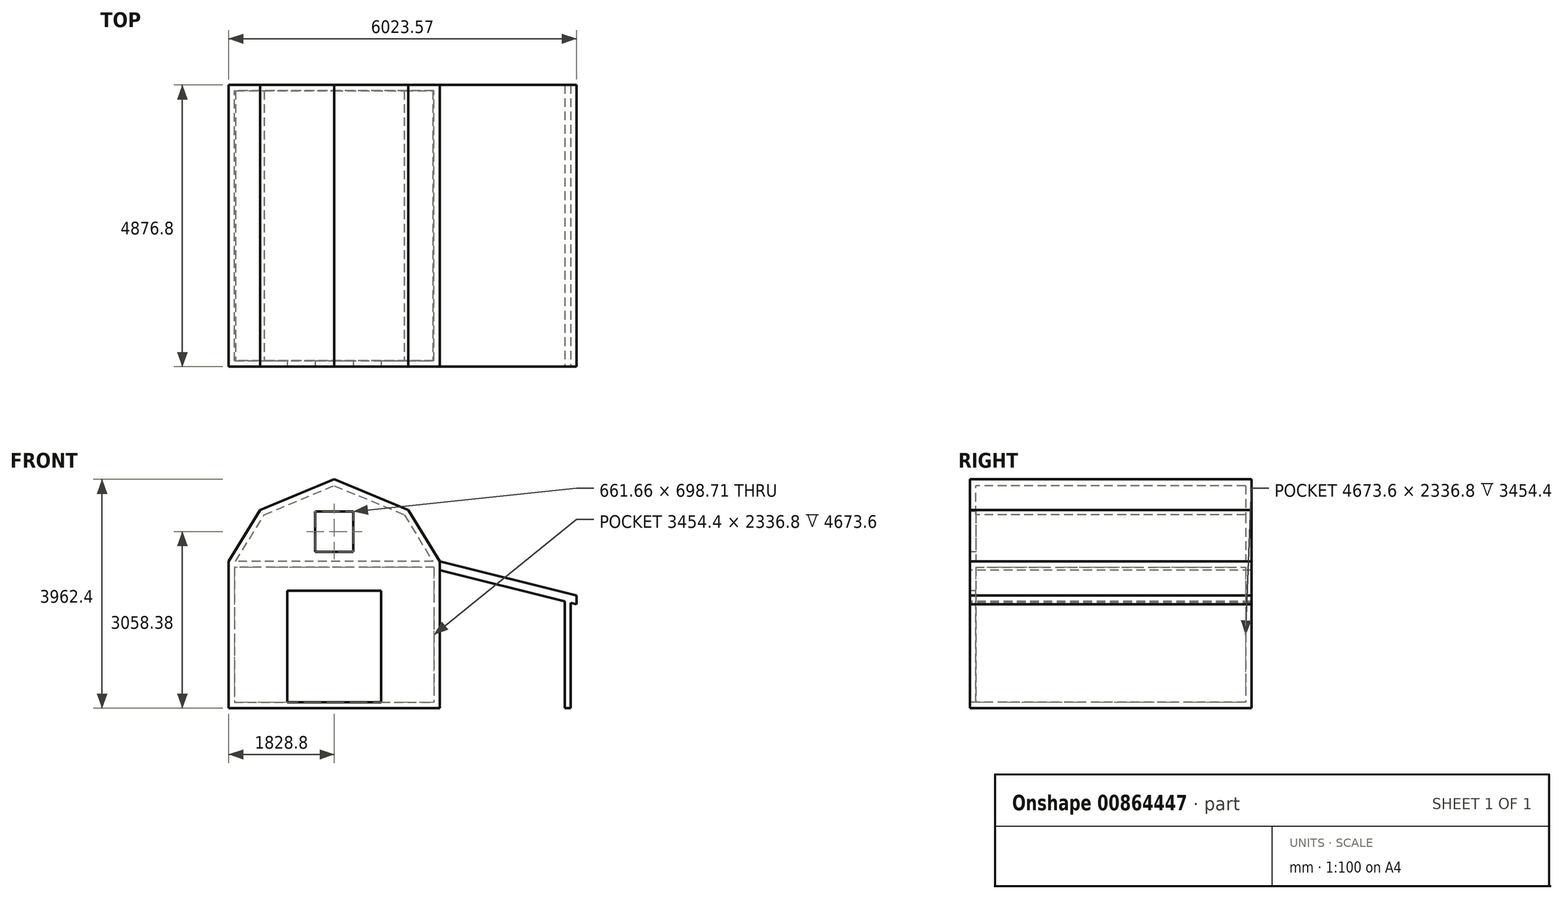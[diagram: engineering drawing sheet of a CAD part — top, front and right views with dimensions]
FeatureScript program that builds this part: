
annotation { "Feature Type Name" : "Feature", "Feature Type Description" : "" }
export const myFeature = defineFeature(function(context is Context, id is Id, definition is map)
    precondition{}
    {
        {
            var Q0;
            Q0=qCreatedBy(makeId("Top.planeOp"),FACE);
            var sketch = newSketch(context, id + "F0", { "sketchPlane" : qUnion([Q0])});
            skLineSegment(sketch, "E0.bottom", {"start": v(-1828.8, 2438.4) * mm, "end": v(1828.8, 2438.4) * mm});
            skLineSegment(sketch, "E0.top", {"start": v(-1828.8, -2438.4) * mm, "end": v(1828.8, -2438.4) * mm});
            skLineSegment(sketch, "E0.left", {"start": v(-1828.8, 2438.4) * mm, "end": v(-1828.8, -2438.4) * mm});
            skLineSegment(sketch, "E0.right", {"start": v(1828.8, 2438.4) * mm, "end": v(1828.8, -2438.4) * mm});
            skPoint(sketch, "E0.middle", {"position": v(0, 0) * mm});
            skSolve(sketch);
        }
        {
            var Q0;
            Q0=makeQuery(id+"F0.imprint","IMPRINT",FACE,{"disambiguationData":[TD([[makeQuery(id+"F0.imprint","IMPRINT",EDGE,{"derivedFrom":sQuery(id+"F0.wireOp",EDGE,"E0.bottom")}),-1.0]])]});
            extrude(context, id + "F1", {"entities" : qUnion([Q0]), "oppositeDirection" : true, "depth" : 101.6 * mm, "offsetDistance" : 30.48 * mm});
        }
        {
            var Q0;
            Q0=makeQuery(id+"F1.opExtrude","CAP_FACE",FACE,{"disambiguationData":[OSD([sQuery(id+"F0.wireOp",EDGE,"E0.bottom"),sQuery(id+"F0.wireOp",EDGE,"E0.top"),sQuery(id+"F0.wireOp",EDGE,"E0.left"),sQuery(id+"F0.wireOp",EDGE,"E0.right")])],"isStart":true});
            var sketch = newSketch(context, id + "F2", { "sketchPlane" : qUnion([Q0])});
            skLineSegment(sketch, "E1.0", {"start": v(-1727.2, 2336.8) * mm, "end": v(1727.2, 2336.8) * mm});
            skLineSegment(sketch, "E1.1", {"start": v(-1727.2, 2336.8) * mm, "end": v(-1727.2, -2336.8) * mm});
            skLineSegment(sketch, "E1.2", {"start": v(-1727.2, -2336.8) * mm, "end": v(1727.2, -2336.8) * mm});
            skLineSegment(sketch, "E1.3", {"start": v(1727.2, 2336.8) * mm, "end": v(1727.2, -2336.8) * mm});
            skSolve(sketch);
        }
        {
            var Q0;
            Q0=makeQuery(id+"F2.imprint","IMPRINT",FACE,{"disambiguationData":[TD([[makeQuery(id+"F2.imprint","IMPRINT",EDGE,{"derivedFrom":sQuery(id+"F2.wireOp",EDGE,"E1.0")}),1.0]])]});
            extrude(context, id + "F3", {"entities" : qUnion([Q0]), "operationType" : NewBodyOperationType.ADD, "depth" : 2438.4 * mm, "offsetDistance" : 30.48 * mm});
        }
        {
            var Q0;
            {var subQ0=sQuery(id+"F0.wireOp",EDGE,"E0.top");Q0=makeQuery(id+"F3.boolean.opBoolean","MERGE",FACE,{"derivedFrom":[makeQuery(id+"F1.opExtrude","SWEPT_FACE",FACE,{"disambiguationData":[OSD([subQ0])]}),makeQuery(id+"F3.opExtrude","SWEPT_FACE",FACE,{"disambiguationData":[OSD([subQ0])]})]});}
            var sketch = newSketch(context, id + "F4", { "sketchPlane" : qUnion([Q0])});
            skLineSegment(sketch, "E2.bottom", {"start": v(0, 0) * mm, "end": v(812.8, 0) * mm});
            skLineSegment(sketch, "E2.top", {"start": v(0, 1930.4) * mm, "end": v(812.8, 1930.4) * mm});
            skLineSegment(sketch, "E2.left", {"start": v(0, 0) * mm, "end": v(0, 1930.4) * mm});
            skLineSegment(sketch, "E2.right", {"start": v(812.8, 0) * mm, "end": v(812.8, 1930.4) * mm});
            skLineSegment(sketch, "E3.bottom", {"start": v(0, 0) * mm, "end": v(-812.8, 0) * mm});
            skLineSegment(sketch, "E3.top", {"start": v(0, 1930.4) * mm, "end": v(-812.8, 1930.4) * mm});
            skLineSegment(sketch, "E3.right", {"start": v(-812.8, 0) * mm, "end": v(-812.8, 1930.4) * mm});
            skSolve(sketch);
        }
        {
            var Q0;
            Q0=makeQuery(id+"F4.imprint","IMPRINT",FACE,{"disambiguationData":[TD([[makeQuery(id+"F4.imprint","IMPRINT",EDGE,{"derivedFrom":sQuery(id+"F4.wireOp",EDGE,"E3.bottom")}),-1.0]])]});
            var Q1;
            Q1=makeQuery(id+"F4.imprint","IMPRINT",FACE,{"disambiguationData":[TD([[makeQuery(id+"F4.imprint","IMPRINT",EDGE,{"derivedFrom":sQuery(id+"F4.wireOp",EDGE,"E2.bottom")}),1.0]])]});
            extrude(context, id + "F5", {"entities" : qUnion([Q0, Q1]), "operationType" : NewBodyOperationType.REMOVE, "oppositeDirection" : true, "depth" : 101.6 * mm, "offsetDistance" : 30.48 * mm});
        }
        {
            var Q0;
            {var subQ0=sQuery(id+"F0.wireOp",EDGE,"E0.top");Q0=makeQuery(id+"F3.boolean.opBoolean","MERGE",FACE,{"derivedFrom":[makeQuery(id+"F1.opExtrude","SWEPT_FACE",FACE,{"disambiguationData":[OSD([subQ0])]}),makeQuery(id+"F3.opExtrude","SWEPT_FACE",FACE,{"disambiguationData":[OSD([subQ0])]})]});}
            var sketch = newSketch(context, id + "F6", { "sketchPlane" : qUnion([Q0])});
            skLineSegment(sketch, "E4", {"start": v(-1828.8, 2438.4) * mm, "end": v(-1282.5, 3330.3) * mm});
            skLineSegment(sketch, "E5", {"start": v(-1282.5, 3330.3) * mm, "end": v(0, 3860.8) * mm});
            skLineSegment(sketch, "E6", {"start": v(0, 3860.8) * mm, "end": v(1282.5, 3330.3) * mm});
            skLineSegment(sketch, "E7", {"start": v(1282.5, 3330.3) * mm, "end": v(1828.8, 2438.4) * mm});
            skLineSegment(sketch, "E8.0", {"start": v(1213.12, 3249.05) * mm, "end": v(1709.66, 2438.4) * mm});
            skLineSegment(sketch, "E8.1", {"start": v(0, 3750.85) * mm, "end": v(1213.12, 3249.05) * mm});
            skLineSegment(sketch, "E8.2", {"start": v(-1213.12, 3249.05) * mm, "end": v(0, 3750.85) * mm});
            skLineSegment(sketch, "E8.3", {"start": v(-1709.66, 2438.4) * mm, "end": v(-1213.12, 3249.05) * mm});
            skLineSegment(sketch, "E9", {"start": v(-1828.8, 2438.4) * mm, "end": v(-1709.66, 2438.4) * mm});
            skLineSegment(sketch, "E10", {"start": v(1709.66, 2438.4) * mm, "end": v(1828.8, 2438.4) * mm});
            skSolve(sketch);
        }
        {
            var Q0;
            Q0=makeQuery(id+"F6.imprint","IMPRINT",FACE,{"disambiguationData":[TD([[makeQuery(id+"F6.imprint","IMPRINT",EDGE,{"derivedFrom":sQuery(id+"F6.wireOp",EDGE,"E4")}),-1.0]])]});
            extrude(context, id + "F7", {"entities" : qUnion([Q0]), "operationType" : NewBodyOperationType.ADD, "oppositeDirection" : true, "depth" : 4876.8 * mm, "offsetDistance" : 30.48 * mm});
        }
        {
            var Q0;
            {var subQ0=sQuery(id+"F0.wireOp",EDGE,"E0.top");Q0=makeQuery(id+"F7.boolean.opBoolean","MERGE",FACE,{"derivedFrom":[makeQuery(id+"F3.boolean.opBoolean","MERGE",FACE,{"derivedFrom":[makeQuery(id+"F1.opExtrude","SWEPT_FACE",FACE,{"disambiguationData":[OSD([subQ0])]}),makeQuery(id+"F3.opExtrude","SWEPT_FACE",FACE,{"disambiguationData":[OSD([subQ0])]})]}),makeQuery(id+"F7.opExtrude","CAP_FACE",FACE,{"disambiguationData":[OSD([sQuery(id+"F6.wireOp",EDGE,"E4"),sQuery(id+"F6.wireOp",EDGE,"E5"),sQuery(id+"F6.wireOp",EDGE,"E6"),sQuery(id+"F6.wireOp",EDGE,"E7"),sQuery(id+"F6.wireOp",EDGE,"E8.0"),sQuery(id+"F6.wireOp",EDGE,"E8.1"),sQuery(id+"F6.wireOp",EDGE,"E8.2"),sQuery(id+"F6.wireOp",EDGE,"E8.3"),sQuery(id+"F6.wireOp",EDGE,"E9"),sQuery(id+"F6.wireOp",EDGE,"E10")])],"isStart":true})]});}
            var sketch = newSketch(context, id + "F8", { "sketchPlane" : qUnion([Q0])});
            skLineSegment(sketch, "E11", {"start": v(-1709.66, 2438.4) * mm, "end": v(-1213.12, 3249.05) * mm});
            skLineSegment(sketch, "E12", {"start": v(-1213.12, 3249.05) * mm, "end": v(0, 3750.85) * mm});
            skLineSegment(sketch, "E13", {"start": v(0, 3750.85) * mm, "end": v(1213.12, 3249.05) * mm});
            skLineSegment(sketch, "E14", {"start": v(1213.12, 3249.05) * mm, "end": v(1709.66, 2438.4) * mm});
            skLineSegment(sketch, "E15", {"start": v(1709.66, 2438.4) * mm, "end": v(-1709.66, 2438.4) * mm});
            skLineSegment(sketch, "E16.bottom", {"start": v(-330.83, 3306.14) * mm, "end": v(330.83, 3306.14) * mm});
            skLineSegment(sketch, "E16.top", {"start": v(-330.83, 2607.43) * mm, "end": v(330.83, 2607.43) * mm});
            skLineSegment(sketch, "E16.left", {"start": v(-330.83, 3306.14) * mm, "end": v(-330.83, 2607.43) * mm});
            skLineSegment(sketch, "E16.right", {"start": v(330.83, 3306.14) * mm, "end": v(330.83, 2607.43) * mm});
            skLineSegment(sketch, "E17", {"start": v(-1213.12, 3249.05) * mm, "end": v(-330.83, 3306.14) * mm});
            skLineSegment(sketch, "E18", {"start": v(1213.12, 3249.05) * mm, "end": v(330.83, 3306.14) * mm});
            skSolve(sketch);
        }
        {
            var Q0;
            Q0=makeQuery(id+"F8.imprint","IMPRINT",FACE,{"disambiguationData":[TD([[makeQuery(id+"F8.imprint","IMPRINT",EDGE,{"derivedFrom":sQuery(id+"F8.wireOp",EDGE,"E11")}),-1.0]])]});
            var Q1;
            Q1=makeQuery(id+"F8.imprint","IMPRINT",FACE,{"disambiguationData":[TD([[makeQuery(id+"F8.imprint","IMPRINT",EDGE,{"derivedFrom":sQuery(id+"F8.wireOp",EDGE,"E12")}),-1.0]])]});
            extrude(context, id + "F9", {"entities" : qUnion([Q0, Q1]), "operationType" : NewBodyOperationType.ADD, "oppositeDirection" : true, "depth" : 101.6 * mm, "offsetDistance" : 30.48 * mm});
        }
        {
            var Q0;
            {var subQ0=sQuery(id+"F0.wireOp",EDGE,"E0.bottom");Q0=makeQuery(id+"F7.boolean.opBoolean","MERGE",FACE,{"derivedFrom":[makeQuery(id+"F3.boolean.opBoolean","MERGE",FACE,{"derivedFrom":[makeQuery(id+"F1.opExtrude","SWEPT_FACE",FACE,{"disambiguationData":[OSD([subQ0])]}),makeQuery(id+"F3.opExtrude","SWEPT_FACE",FACE,{"disambiguationData":[OSD([subQ0])]})]}),makeQuery(id+"F7.opExtrude","CAP_FACE",FACE,{"disambiguationData":[OSD([sQuery(id+"F6.wireOp",EDGE,"E4"),sQuery(id+"F6.wireOp",EDGE,"E5"),sQuery(id+"F6.wireOp",EDGE,"E6"),sQuery(id+"F6.wireOp",EDGE,"E7"),sQuery(id+"F6.wireOp",EDGE,"E8.0"),sQuery(id+"F6.wireOp",EDGE,"E8.1"),sQuery(id+"F6.wireOp",EDGE,"E8.2"),sQuery(id+"F6.wireOp",EDGE,"E8.3"),sQuery(id+"F6.wireOp",EDGE,"E9"),sQuery(id+"F6.wireOp",EDGE,"E10")])],"isStart":false})]});}
            var sketch = newSketch(context, id + "F10", { "sketchPlane" : qUnion([Q0])});
            skLineSegment(sketch, "E19", {"start": v(-1709.66, 2438.4) * mm, "end": v(-1213.12, 3249.05) * mm});
            skLineSegment(sketch, "E20", {"start": v(-1213.12, 3249.05) * mm, "end": v(0, 3750.85) * mm});
            skLineSegment(sketch, "E21", {"start": v(0, 3750.85) * mm, "end": v(1213.12, 3249.05) * mm});
            skLineSegment(sketch, "E22", {"start": v(1213.12, 3249.05) * mm, "end": v(1709.66, 2438.4) * mm});
            skLineSegment(sketch, "E23", {"start": v(1709.66, 2438.4) * mm, "end": v(-1709.66, 2438.4) * mm});
            skSolve(sketch);
        }
        {
            var Q0;
            Q0=makeQuery(id+"F10.imprint","IMPRINT",FACE,{"disambiguationData":[TD([[makeQuery(id+"F10.imprint","IMPRINT",EDGE,{"derivedFrom":sQuery(id+"F10.wireOp",EDGE,"E19")}),1.0]])]});
            extrude(context, id + "F11", {"entities" : qUnion([Q0]), "operationType" : NewBodyOperationType.ADD, "oppositeDirection" : true, "depth" : 101.6 * mm, "offsetDistance" : 30.48 * mm});
        }
        {
            var Q0;
            {var subQ0=sQuery(id+"F0.wireOp",EDGE,"E0.top");Q0=makeQuery(id+"F9.boolean.opBoolean","MERGE",FACE,{"derivedFrom":[makeQuery(id+"F7.boolean.opBoolean","MERGE",FACE,{"derivedFrom":[makeQuery(id+"F3.boolean.opBoolean","MERGE",FACE,{"derivedFrom":[makeQuery(id+"F1.opExtrude","SWEPT_FACE",FACE,{"disambiguationData":[OSD([subQ0])]}),makeQuery(id+"F3.opExtrude","SWEPT_FACE",FACE,{"disambiguationData":[OSD([subQ0])]})]}),makeQuery(id+"F7.opExtrude","CAP_FACE",FACE,{"disambiguationData":[OSD([sQuery(id+"F6.wireOp",EDGE,"E4"),sQuery(id+"F6.wireOp",EDGE,"E5"),sQuery(id+"F6.wireOp",EDGE,"E6"),sQuery(id+"F6.wireOp",EDGE,"E7"),sQuery(id+"F6.wireOp",EDGE,"E8.0"),sQuery(id+"F6.wireOp",EDGE,"E8.1"),sQuery(id+"F6.wireOp",EDGE,"E8.2"),sQuery(id+"F6.wireOp",EDGE,"E8.3"),sQuery(id+"F6.wireOp",EDGE,"E9"),sQuery(id+"F6.wireOp",EDGE,"E10")])],"isStart":true})]}),makeQuery(id+"F9.opExtrude","CAP_FACE",FACE,{"disambiguationData":[OSD([sQuery(id+"F8.wireOp",EDGE,"E11"),sQuery(id+"F8.wireOp",EDGE,"E12"),sQuery(id+"F8.wireOp",EDGE,"E13"),sQuery(id+"F8.wireOp",EDGE,"E14"),sQuery(id+"F8.wireOp",EDGE,"E15"),sQuery(id+"F8.wireOp",EDGE,"E16.bottom"),sQuery(id+"F8.wireOp",EDGE,"E16.top"),sQuery(id+"F8.wireOp",EDGE,"E16.left"),sQuery(id+"F8.wireOp",EDGE,"E16.right")])],"isStart":true})]});}
            var sketch = newSketch(context, id + "F12", { "sketchPlane" : qUnion([Q0])});
            skLineSegment(sketch, "E24.bottom", {"start": v(-1828.8, 2438.4) * mm, "end": v(1828.8, 2438.4) * mm});
            skLineSegment(sketch, "E24.top", {"start": v(-1828.8, 2336.8) * mm, "end": v(1828.8, 2336.8) * mm});
            skLineSegment(sketch, "E24.left", {"start": v(-1828.8, 2438.4) * mm, "end": v(-1828.8, 2336.8) * mm});
            skLineSegment(sketch, "E24.right", {"start": v(1828.8, 2438.4) * mm, "end": v(1828.8, 2336.8) * mm});
            skSolve(sketch);
        }
        {
            var Q0;
            Q0=makeQuery(id+"F12.imprint","IMPRINT",FACE,{"disambiguationData":[TD([[makeQuery(id+"F12.imprint","IMPRINT",EDGE,{"derivedFrom":sQuery(id+"F12.wireOp",EDGE,"E24.bottom")}),-1.0]])]});
            extrude(context, id + "F13", {"entities" : qUnion([Q0]), "operationType" : NewBodyOperationType.ADD, "oppositeDirection" : true, "depth" : 4876.8 * mm, "offsetDistance" : 30.48 * mm});
        }
        {
            var Q0;
            {var subQ0=sQuery(id+"F0.wireOp",EDGE,"E0.top");Q0=makeQuery(id+"F9.boolean.opBoolean","MERGE",FACE,{"derivedFrom":[makeQuery(id+"F7.boolean.opBoolean","MERGE",FACE,{"derivedFrom":[makeQuery(id+"F3.boolean.opBoolean","MERGE",FACE,{"derivedFrom":[makeQuery(id+"F1.opExtrude","SWEPT_FACE",FACE,{"disambiguationData":[OSD([subQ0])]}),makeQuery(id+"F3.opExtrude","SWEPT_FACE",FACE,{"disambiguationData":[OSD([subQ0])]})]}),makeQuery(id+"F7.opExtrude","CAP_FACE",FACE,{"disambiguationData":[OSD([sQuery(id+"F6.wireOp",EDGE,"E4"),sQuery(id+"F6.wireOp",EDGE,"E5"),sQuery(id+"F6.wireOp",EDGE,"E6"),sQuery(id+"F6.wireOp",EDGE,"E7"),sQuery(id+"F6.wireOp",EDGE,"E8.0"),sQuery(id+"F6.wireOp",EDGE,"E8.1"),sQuery(id+"F6.wireOp",EDGE,"E8.2"),sQuery(id+"F6.wireOp",EDGE,"E8.3"),sQuery(id+"F6.wireOp",EDGE,"E9"),sQuery(id+"F6.wireOp",EDGE,"E10")])],"isStart":true})]}),makeQuery(id+"F9.opExtrude","CAP_FACE",FACE,{"disambiguationData":[OSD([sQuery(id+"F8.wireOp",EDGE,"E11"),sQuery(id+"F8.wireOp",EDGE,"E12"),sQuery(id+"F8.wireOp",EDGE,"E13"),sQuery(id+"F8.wireOp",EDGE,"E14"),sQuery(id+"F8.wireOp",EDGE,"E15"),sQuery(id+"F8.wireOp",EDGE,"E16.bottom"),sQuery(id+"F8.wireOp",EDGE,"E16.top"),sQuery(id+"F8.wireOp",EDGE,"E16.left"),sQuery(id+"F8.wireOp",EDGE,"E16.right")])],"isStart":true})]});}
            var sketch = newSketch(context, id + "F14", { "sketchPlane" : qUnion([Q0])});
            skLineSegment(sketch, "E25.bottom", {"start": v(1828.8, 2438.4) * mm, "end": v(4194.77, 1848.5) * mm});
            skLineSegment(sketch, "E26", {"start": v(1828.8, 2438.4) * mm, "end": v(1828.8, 2286) * mm});
            skLineSegment(sketch, "E27", {"start": v(1828.8, 2286) * mm, "end": v(4194.77, 1696.1) * mm});
            skLineSegment(sketch, "E28", {"start": v(4194.77, 1696.1) * mm, "end": v(4194.77, 1848.5) * mm});
            skSolve(sketch);
        }
        {
            var Q0;
            Q0=makeQuery(id+"F14.imprint","IMPRINT",FACE,{"disambiguationData":[TD([[makeQuery(id+"F14.imprint","IMPRINT",EDGE,{"derivedFrom":sQuery(id+"F14.wireOp",EDGE,"E25.bottom")}),-1.0]])]});
            extrude(context, id + "F15", {"entities" : qUnion([Q0]), "oppositeDirection" : true, "depth" : 4876.8 * mm, "offsetDistance" : 30.48 * mm});
        }
        {
            var Q0;
            Q0=makeQuery(id+"F15.opExtrude","SWEPT_BODY",BODY,{"disambiguationData":[OSD([sQuery(id+"F14.wireOp",EDGE,"E25.bottom"),sQuery(id+"F14.wireOp",EDGE,"E26"),sQuery(id+"F14.wireOp",EDGE,"E27"),sQuery(id+"F14.wireOp",EDGE,"E28")])]});
            deleteBodies(context, id + "F16", {"entities" : qUnion([Q0])});
        }
        {
            var Q0;
            {var subQ0=sQuery(id+"F0.wireOp",EDGE,"E0.top");Q0=makeQuery(id+"F9.boolean.opBoolean","MERGE",FACE,{"derivedFrom":[makeQuery(id+"F7.boolean.opBoolean","MERGE",FACE,{"derivedFrom":[makeQuery(id+"F3.boolean.opBoolean","MERGE",FACE,{"derivedFrom":[makeQuery(id+"F1.opExtrude","SWEPT_FACE",FACE,{"disambiguationData":[OSD([subQ0])]}),makeQuery(id+"F3.opExtrude","SWEPT_FACE",FACE,{"disambiguationData":[OSD([subQ0])]})]}),makeQuery(id+"F7.opExtrude","CAP_FACE",FACE,{"disambiguationData":[OSD([sQuery(id+"F6.wireOp",EDGE,"E4"),sQuery(id+"F6.wireOp",EDGE,"E5"),sQuery(id+"F6.wireOp",EDGE,"E6"),sQuery(id+"F6.wireOp",EDGE,"E7"),sQuery(id+"F6.wireOp",EDGE,"E8.0"),sQuery(id+"F6.wireOp",EDGE,"E8.1"),sQuery(id+"F6.wireOp",EDGE,"E8.2"),sQuery(id+"F6.wireOp",EDGE,"E8.3"),sQuery(id+"F6.wireOp",EDGE,"E9"),sQuery(id+"F6.wireOp",EDGE,"E10")])],"isStart":true})]}),makeQuery(id+"F9.opExtrude","CAP_FACE",FACE,{"disambiguationData":[OSD([sQuery(id+"F8.wireOp",EDGE,"E11"),sQuery(id+"F8.wireOp",EDGE,"E12"),sQuery(id+"F8.wireOp",EDGE,"E13"),sQuery(id+"F8.wireOp",EDGE,"E14"),sQuery(id+"F8.wireOp",EDGE,"E15"),sQuery(id+"F8.wireOp",EDGE,"E16.bottom"),sQuery(id+"F8.wireOp",EDGE,"E16.top"),sQuery(id+"F8.wireOp",EDGE,"E16.left"),sQuery(id+"F8.wireOp",EDGE,"E16.right")])],"isStart":true})]});}
            var sketch = newSketch(context, id + "F17", { "sketchPlane" : qUnion([Q0])});
            skLineSegment(sketch, "E29", {"start": v(1828.8, 2438.4) * mm, "end": v(4194.77, 1848.5) * mm});
            skLineSegment(sketch, "E30", {"start": v(1828.8, 2438.4) * mm, "end": v(1828.8, 2286) * mm});
            skLineSegment(sketch, "E31", {"start": v(1828.8, 2286) * mm, "end": v(4194.77, 1696.1) * mm});
            skLineSegment(sketch, "E32", {"start": v(4194.77, 1696.1) * mm, "end": v(4194.77, 1848.5) * mm});
            skLineSegment(sketch, "E33", {"start": v(4093.17, 1721.43) * mm, "end": v(4093.17, -101.6) * mm});
            skLineSegment(sketch, "E34", {"start": v(3991.57, 1746.76) * mm, "end": v(3991.57, -101.6) * mm});
            skLineSegment(sketch, "E35", {"start": v(3991.57, -101.6) * mm, "end": v(4093.17, -101.6) * mm});
            skSolve(sketch);
        }
        {
            var Q0;
            Q0=makeQuery(id+"F17.imprint","IMPRINT",FACE,{"disambiguationData":[TD([[makeQuery(id+"F17.imprint","IMPRINT",EDGE,{"derivedFrom":sQuery(id+"F17.wireOp",EDGE,"E29")}),-1.0]])]});
            var Q1;
            {var subQ0=sQuery(id+"F17.wireOp",EDGE,"E33");Q1=makeQuery(id+"F17.imprint","IMPRINT",FACE,{"disambiguationData":[TD([[makeQuery(id+"F17.imprint","IMPRINT",EDGE,{"derivedFrom":subQ0}),-1.0]])]});}
            extrude(context, id + "F18", {"entities" : qUnion([Q0, Q1]), "oppositeDirection" : true, "depth" : 4876.8 * mm, "offsetDistance" : 30.48 * mm});
        }
    });
